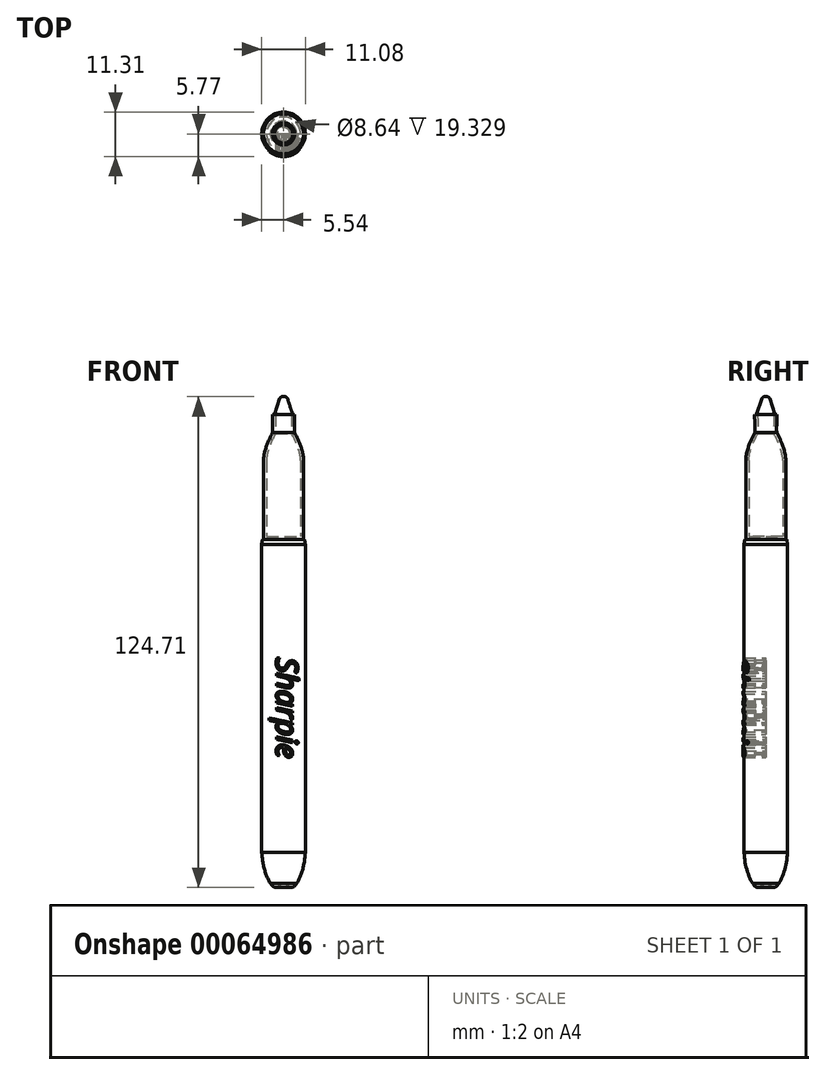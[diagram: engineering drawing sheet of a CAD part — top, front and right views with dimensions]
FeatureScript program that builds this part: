
annotation { "Feature Type Name" : "Feature", "Feature Type Description" : "" }
export const myFeature = defineFeature(function(context is Context, id is Id, definition is map)
    precondition{}
    {
        {
            var Q0;
            Q0=qCreatedBy(makeId("Right.planeOp"),FACE);
            var sketch = newSketch(context, id + "F0", { "sketchPlane" : qUnion([Q0])});
            skArc(sketch, "E0", {"start": v(1.65, 0) * mm, "mid": v(0.9, 0.63) * mm, "end": v(0, 1.02) * mm});
            skLineSegment(sketch, "E1", {"start": v(0, 0) * mm, "end": v(0, 15.3) * mm, "construction": true});
            skLineSegment(sketch, "E2", {"start": v(-4.14, 8.9) * mm, "end": v(12.15, 8.9) * mm, "construction": true});
            skLineSegment(sketch, "E3", {"start": v(5.54, -3.16) * mm, "end": v(5.54, 13.42) * mm, "construction": true});
            skLineSegment(sketch, "E4", {"start": v(3.31, 16.2) * mm, "end": v(3.31, -2.19) * mm, "construction": true});
            skFitSpline(sketch, "E5", {"points": [v(1.65, 0) * mm, v(3.31, 1.03) * mm], "startDerivative": vector(2.74, 0) * mm, "endDerivative": vector(1.4, 2.31) * mm});
            skFitSpline(sketch, "E6", {"points": [v(3.31, 1.03) * mm, v(5.54, 8.9) * mm], "startDerivative": vector(3.92, 5.98) * mm, "endDerivative": vector(0.67, 9.24) * mm});
            skLineSegment(sketch, "E7", {"start": v(-15.24, 87.12) * mm, "end": v(35.45, 87.12) * mm, "construction": true});
            skLineSegment(sketch, "E8", {"start": v(5.54, 8.9) * mm, "end": v(5.54, 87.12) * mm});
            skPoint(sketch, "E8.endSnap0", {"position": v(10.1, 87.12) * mm});
            skLineSegment(sketch, "E9", {"start": v(5.54, 87.12) * mm, "end": v(5.33, 88.38) * mm});
            skLineSegment(sketch, "E10", {"start": v(5.33, 88.38) * mm, "end": v(0, 88.38) * mm});
            skLineSegment(sketch, "E11", {"start": v(0, 88.38) * mm, "end": v(0, 1.02) * mm});
            skSolve(sketch);
        }
        {
            var Q0;
            Q0 = qSketchRegion(id + "F0", true);
            var Q1;
            Q1=sQuery(id+"F0.wireOp",EDGE,"E11");
            revolve(context, id + "F1", {"entities" : qUnion([Q0]), "axis" : qUnion([Q1]), "revolveType" : RevolveType.FULL});
        }
        {
            var Q0;
            Q0=qCreatedBy(makeId("Front.planeOp"),FACE);
            var sketch = newSketch(context, id + "F2", { "sketchPlane" : qUnion([Q0])});
            skLineSegment(sketch, "E12", {"start": v(0, 88.38) * mm, "end": v(0, 120.13) * mm});
            skLineSegment(sketch, "E13", {"start": v(0, 120.13) * mm, "end": v(2.8, 120.13) * mm});
            skLineSegment(sketch, "E14", {"start": v(-7.77, 108.47) * mm, "end": v(20.65, 108.47) * mm, "construction": true});
            skLineSegment(sketch, "E15", {"start": v(5.08, 128.73) * mm, "end": v(5.08, 79.74) * mm, "construction": true});
            skLineSegment(sketch, "E16", {"start": v(5.08, 79.74) * mm, "end": v(5.61, 79.74) * mm, "construction": true});
            skLineSegment(sketch, "E17", {"start": v(0, 88.38) * mm, "end": v(5.08, 88.38) * mm});
            skLineSegment(sketch, "E18", {"start": v(5.08, 88.38) * mm, "end": v(5.08, 108.47) * mm});
            skFitSpline(sketch, "E19", {"points": [v(2.8, 115.55) * mm, v(5.08, 108.47) * mm], "startDerivative": vector(4.16, -7.76) * mm, "endDerivative": vector(0, -5.98) * mm});
            skFitSpline(sketch, "E20", {"points": [v(2.8, 120.13) * mm, v(2.8, 115.55) * mm], "startDerivative": vector(0.35, -1.11) * mm, "endDerivative": vector(0.39, -3.2) * mm});
            skSolve(sketch);
        }
        {
            var Q0;
            Q0=makeQuery(id+"F2.imprint","IMPRINT",FACE,{"disambiguationData":[TD([[makeQuery(id+"F2.imprint","IMPRINT",EDGE,{"derivedFrom":sQuery(id+"F2.wireOp",EDGE,"E12")}),-1.0]])]});
            var Q1;
            Q1=sQuery(id+"F2.wireOp",EDGE,"E12");
            revolve(context, id + "F3", {"entities" : qUnion([Q0]), "axis" : qUnion([Q1]), "revolveType" : RevolveType.FULL});
        }
        {
            var Q0;
            Q0=makeQuery(id+"F3.opRevolve","SWEPT_FACE",FACE,{"disambiguationData":[OSD([sQuery(id+"F2.wireOp",EDGE,"E13")])]});
            shell(context, id + "F4", {"entities" : qUnion([Q0]), "thickness" : 0.76 * mm});
        }
        {
            var Q0;
            Q0=qCreatedBy(makeId("Front.planeOp"),FACE);
            var sketch = newSketch(context, id + "F5", { "sketchPlane" : qUnion([Q0])});
            skText(sketch, "E21", { "text": "Sharpie", "fontName": "OpenSans-Italic.ttf"});
            const initialGuessF5  = {"E21": [-0.00997, 0.02356, 1, 0, 0.00548]};
            skSetInitialGuess(sketch, initialGuessF5);
            skSolve(sketch);
        }
        {
            var Q0;
            Q0 = qSketchRegion(id + "F5", true);
            extrude(context, id + "F6", {"entities" : qUnion([Q0]), "depth" : 6.35 * mm});
        }
        {
            var Q0;
            Q0=qCreatedBy(makeId("Front.planeOp"),FACE);
            var sketch = newSketch(context, id + "F7", { "sketchPlane" : qUnion([Q0])});
            skLineSegment(sketch, "E22", {"start": v(0, 0) * mm, "end": v(0, 153.56) * mm, "construction": true});
            skLineSegment(sketch, "E23", {"start": v(0, 0) * mm, "end": v(-98.51, 0) * mm, "construction": true});
            skSolve(sketch);
        }
        {
            var Q0;
            Q0=qCreatedBy(makeId("Top.planeOp"),FACE);
            var sketch = newSketch(context, id + "F8", { "sketchPlane" : qUnion([Q0])});
            skLineSegment(sketch, "E24", {"start": v(0, 0) * mm, "end": v(0, 70.55) * mm, "construction": true});
            skSolve(sketch);
        }
        {
            var Q0;
            Q0=makeQuery(id+"F6.opExtrude","SWEPT_BODY",BODY,{"disambiguationData":[OSD([sQuery(id+"F5.wireOp",EDGE,"E21.sketch_text.stroke-126"),sQuery(id+"F5.wireOp",EDGE,"E21.sketch_text.stroke-127"),sQuery(id+"F5.wireOp",EDGE,"E21.sketch_text.stroke-128"),sQuery(id+"F5.wireOp",EDGE,"E21.sketch_text.stroke-129"),sQuery(id+"F5.wireOp",EDGE,"E21.sketch_text.stroke-130"),sQuery(id+"F5.wireOp",EDGE,"E21.sketch_text.stroke-131"),sQuery(id+"F5.wireOp",EDGE,"E21.sketch_text.stroke-132"),sQuery(id+"F5.wireOp",EDGE,"E21.sketch_text.stroke-133"),sQuery(id+"F5.wireOp",EDGE,"E21.sketch_text.stroke-134"),sQuery(id+"F5.wireOp",EDGE,"E21.sketch_text.stroke-135"),sQuery(id+"F5.wireOp",EDGE,"E21.sketch_text.stroke-136"),sQuery(id+"F5.wireOp",EDGE,"E21.sketch_text.stroke-137"),sQuery(id+"F5.wireOp",EDGE,"E21.sketch_text.stroke-138"),sQuery(id+"F5.wireOp",EDGE,"E21.sketch_text.stroke-139"),sQuery(id+"F5.wireOp",EDGE,"E21.sketch_text.stroke-140"),sQuery(id+"F5.wireOp",EDGE,"E21.sketch_text.stroke-141"),sQuery(id+"F5.wireOp",EDGE,"E21.sketch_text.stroke-142"),sQuery(id+"F5.wireOp",EDGE,"E21.sketch_text.stroke-143"),sQuery(id+"F5.wireOp",EDGE,"E21.sketch_text.stroke-144"),sQuery(id+"F5.wireOp",EDGE,"E21.sketch_text.stroke-145"),sQuery(id+"F5.wireOp",EDGE,"E21.sketch_text.stroke-146"),sQuery(id+"F5.wireOp",EDGE,"E21.sketch_text.stroke-147"),sQuery(id+"F5.wireOp",EDGE,"E21.sketch_text.stroke-148"),sQuery(id+"F5.wireOp",EDGE,"E21.sketch_text.stroke-149"),sQuery(id+"F5.wireOp",EDGE,"E21.sketch_text.stroke-150")])]});
            var Q1;
            Q1=makeQuery(id+"F6.opExtrude","SWEPT_BODY",BODY,{"disambiguationData":[OSD([sQuery(id+"F5.wireOp",EDGE,"E21.sketch_text.stroke-119"),sQuery(id+"F5.wireOp",EDGE,"E21.sketch_text.stroke-120"),sQuery(id+"F5.wireOp",EDGE,"E21.sketch_text.stroke-121"),sQuery(id+"F5.wireOp",EDGE,"E21.sketch_text.stroke-122"),sQuery(id+"F5.wireOp",EDGE,"E21.sketch_text.stroke-123"),sQuery(id+"F5.wireOp",EDGE,"E21.sketch_text.stroke-124"),sQuery(id+"F5.wireOp",EDGE,"E21.sketch_text.stroke-125")])]});
            var Q2;
            Q2=makeQuery(id+"F6.opExtrude","SWEPT_BODY",BODY,{"disambiguationData":[OSD([sQuery(id+"F5.wireOp",EDGE,"E21.sketch_text.stroke-115"),sQuery(id+"F5.wireOp",EDGE,"E21.sketch_text.stroke-116"),sQuery(id+"F5.wireOp",EDGE,"E21.sketch_text.stroke-117"),sQuery(id+"F5.wireOp",EDGE,"E21.sketch_text.stroke-118")])]});
            var Q3;
            Q3=makeQuery(id+"F6.opExtrude","SWEPT_BODY",BODY,{"disambiguationData":[OSD([sQuery(id+"F5.wireOp",EDGE,"E21.sketch_text.stroke-89"),sQuery(id+"F5.wireOp",EDGE,"E21.sketch_text.stroke-90"),sQuery(id+"F5.wireOp",EDGE,"E21.sketch_text.stroke-91"),sQuery(id+"F5.wireOp",EDGE,"E21.sketch_text.stroke-92"),sQuery(id+"F5.wireOp",EDGE,"E21.sketch_text.stroke-93"),sQuery(id+"F5.wireOp",EDGE,"E21.sketch_text.stroke-94"),sQuery(id+"F5.wireOp",EDGE,"E21.sketch_text.stroke-95"),sQuery(id+"F5.wireOp",EDGE,"E21.sketch_text.stroke-96"),sQuery(id+"F5.wireOp",EDGE,"E21.sketch_text.stroke-97"),sQuery(id+"F5.wireOp",EDGE,"E21.sketch_text.stroke-98"),sQuery(id+"F5.wireOp",EDGE,"E21.sketch_text.stroke-99"),sQuery(id+"F5.wireOp",EDGE,"E21.sketch_text.stroke-100"),sQuery(id+"F5.wireOp",EDGE,"E21.sketch_text.stroke-101"),sQuery(id+"F5.wireOp",EDGE,"E21.sketch_text.stroke-102"),sQuery(id+"F5.wireOp",EDGE,"E21.sketch_text.stroke-103"),sQuery(id+"F5.wireOp",EDGE,"E21.sketch_text.stroke-104"),sQuery(id+"F5.wireOp",EDGE,"E21.sketch_text.stroke-105"),sQuery(id+"F5.wireOp",EDGE,"E21.sketch_text.stroke-106"),sQuery(id+"F5.wireOp",EDGE,"E21.sketch_text.stroke-107"),sQuery(id+"F5.wireOp",EDGE,"E21.sketch_text.stroke-108"),sQuery(id+"F5.wireOp",EDGE,"E21.sketch_text.stroke-109"),sQuery(id+"F5.wireOp",EDGE,"E21.sketch_text.stroke-110"),sQuery(id+"F5.wireOp",EDGE,"E21.sketch_text.stroke-111"),sQuery(id+"F5.wireOp",EDGE,"E21.sketch_text.stroke-112"),sQuery(id+"F5.wireOp",EDGE,"E21.sketch_text.stroke-113"),sQuery(id+"F5.wireOp",EDGE,"E21.sketch_text.stroke-114")])]});
            var Q4;
            Q4=makeQuery(id+"F6.opExtrude","SWEPT_BODY",BODY,{"disambiguationData":[OSD([sQuery(id+"F5.wireOp",EDGE,"E21.sketch_text.stroke-74"),sQuery(id+"F5.wireOp",EDGE,"E21.sketch_text.stroke-75"),sQuery(id+"F5.wireOp",EDGE,"E21.sketch_text.stroke-76"),sQuery(id+"F5.wireOp",EDGE,"E21.sketch_text.stroke-77"),sQuery(id+"F5.wireOp",EDGE,"E21.sketch_text.stroke-78"),sQuery(id+"F5.wireOp",EDGE,"E21.sketch_text.stroke-79"),sQuery(id+"F5.wireOp",EDGE,"E21.sketch_text.stroke-80"),sQuery(id+"F5.wireOp",EDGE,"E21.sketch_text.stroke-81"),sQuery(id+"F5.wireOp",EDGE,"E21.sketch_text.stroke-82"),sQuery(id+"F5.wireOp",EDGE,"E21.sketch_text.stroke-83"),sQuery(id+"F5.wireOp",EDGE,"E21.sketch_text.stroke-84"),sQuery(id+"F5.wireOp",EDGE,"E21.sketch_text.stroke-85"),sQuery(id+"F5.wireOp",EDGE,"E21.sketch_text.stroke-86"),sQuery(id+"F5.wireOp",EDGE,"E21.sketch_text.stroke-87"),sQuery(id+"F5.wireOp",EDGE,"E21.sketch_text.stroke-88")])]});
            var Q5;
            Q5=makeQuery(id+"F6.opExtrude","SWEPT_BODY",BODY,{"disambiguationData":[OSD([sQuery(id+"F5.wireOp",EDGE,"E21.sketch_text.stroke-49"),sQuery(id+"F5.wireOp",EDGE,"E21.sketch_text.stroke-50"),sQuery(id+"F5.wireOp",EDGE,"E21.sketch_text.stroke-51"),sQuery(id+"F5.wireOp",EDGE,"E21.sketch_text.stroke-52"),sQuery(id+"F5.wireOp",EDGE,"E21.sketch_text.stroke-53"),sQuery(id+"F5.wireOp",EDGE,"E21.sketch_text.stroke-54"),sQuery(id+"F5.wireOp",EDGE,"E21.sketch_text.stroke-55"),sQuery(id+"F5.wireOp",EDGE,"E21.sketch_text.stroke-56"),sQuery(id+"F5.wireOp",EDGE,"E21.sketch_text.stroke-57"),sQuery(id+"F5.wireOp",EDGE,"E21.sketch_text.stroke-58"),sQuery(id+"F5.wireOp",EDGE,"E21.sketch_text.stroke-59"),sQuery(id+"F5.wireOp",EDGE,"E21.sketch_text.stroke-60"),sQuery(id+"F5.wireOp",EDGE,"E21.sketch_text.stroke-61"),sQuery(id+"F5.wireOp",EDGE,"E21.sketch_text.stroke-62"),sQuery(id+"F5.wireOp",EDGE,"E21.sketch_text.stroke-63"),sQuery(id+"F5.wireOp",EDGE,"E21.sketch_text.stroke-64"),sQuery(id+"F5.wireOp",EDGE,"E21.sketch_text.stroke-65"),sQuery(id+"F5.wireOp",EDGE,"E21.sketch_text.stroke-66"),sQuery(id+"F5.wireOp",EDGE,"E21.sketch_text.stroke-67"),sQuery(id+"F5.wireOp",EDGE,"E21.sketch_text.stroke-68"),sQuery(id+"F5.wireOp",EDGE,"E21.sketch_text.stroke-69"),sQuery(id+"F5.wireOp",EDGE,"E21.sketch_text.stroke-70"),sQuery(id+"F5.wireOp",EDGE,"E21.sketch_text.stroke-71"),sQuery(id+"F5.wireOp",EDGE,"E21.sketch_text.stroke-72"),sQuery(id+"F5.wireOp",EDGE,"E21.sketch_text.stroke-73")])]});
            var Q6;
            Q6=makeQuery(id+"F6.opExtrude","SWEPT_BODY",BODY,{"disambiguationData":[OSD([sQuery(id+"F5.wireOp",EDGE,"E21.sketch_text.stroke-27"),sQuery(id+"F5.wireOp",EDGE,"E21.sketch_text.stroke-28"),sQuery(id+"F5.wireOp",EDGE,"E21.sketch_text.stroke-29"),sQuery(id+"F5.wireOp",EDGE,"E21.sketch_text.stroke-30"),sQuery(id+"F5.wireOp",EDGE,"E21.sketch_text.stroke-31"),sQuery(id+"F5.wireOp",EDGE,"E21.sketch_text.stroke-32"),sQuery(id+"F5.wireOp",EDGE,"E21.sketch_text.stroke-33"),sQuery(id+"F5.wireOp",EDGE,"E21.sketch_text.stroke-34"),sQuery(id+"F5.wireOp",EDGE,"E21.sketch_text.stroke-35"),sQuery(id+"F5.wireOp",EDGE,"E21.sketch_text.stroke-36"),sQuery(id+"F5.wireOp",EDGE,"E21.sketch_text.stroke-37"),sQuery(id+"F5.wireOp",EDGE,"E21.sketch_text.stroke-38"),sQuery(id+"F5.wireOp",EDGE,"E21.sketch_text.stroke-39"),sQuery(id+"F5.wireOp",EDGE,"E21.sketch_text.stroke-40"),sQuery(id+"F5.wireOp",EDGE,"E21.sketch_text.stroke-41"),sQuery(id+"F5.wireOp",EDGE,"E21.sketch_text.stroke-42"),sQuery(id+"F5.wireOp",EDGE,"E21.sketch_text.stroke-43"),sQuery(id+"F5.wireOp",EDGE,"E21.sketch_text.stroke-44"),sQuery(id+"F5.wireOp",EDGE,"E21.sketch_text.stroke-45"),sQuery(id+"F5.wireOp",EDGE,"E21.sketch_text.stroke-46"),sQuery(id+"F5.wireOp",EDGE,"E21.sketch_text.stroke-47"),sQuery(id+"F5.wireOp",EDGE,"E21.sketch_text.stroke-48")])]});
            var Q7;
            Q7=makeQuery(id+"F6.opExtrude","SWEPT_BODY",BODY,{"disambiguationData":[OSD([sQuery(id+"F5.wireOp",EDGE,"E21.sketch_text.stroke-0"),sQuery(id+"F5.wireOp",EDGE,"E21.sketch_text.stroke-1"),sQuery(id+"F5.wireOp",EDGE,"E21.sketch_text.stroke-2"),sQuery(id+"F5.wireOp",EDGE,"E21.sketch_text.stroke-3"),sQuery(id+"F5.wireOp",EDGE,"E21.sketch_text.stroke-4"),sQuery(id+"F5.wireOp",EDGE,"E21.sketch_text.stroke-5"),sQuery(id+"F5.wireOp",EDGE,"E21.sketch_text.stroke-6"),sQuery(id+"F5.wireOp",EDGE,"E21.sketch_text.stroke-7"),sQuery(id+"F5.wireOp",EDGE,"E21.sketch_text.stroke-8"),sQuery(id+"F5.wireOp",EDGE,"E21.sketch_text.stroke-9"),sQuery(id+"F5.wireOp",EDGE,"E21.sketch_text.stroke-10"),sQuery(id+"F5.wireOp",EDGE,"E21.sketch_text.stroke-11"),sQuery(id+"F5.wireOp",EDGE,"E21.sketch_text.stroke-12"),sQuery(id+"F5.wireOp",EDGE,"E21.sketch_text.stroke-13"),sQuery(id+"F5.wireOp",EDGE,"E21.sketch_text.stroke-14"),sQuery(id+"F5.wireOp",EDGE,"E21.sketch_text.stroke-15"),sQuery(id+"F5.wireOp",EDGE,"E21.sketch_text.stroke-16"),sQuery(id+"F5.wireOp",EDGE,"E21.sketch_text.stroke-17"),sQuery(id+"F5.wireOp",EDGE,"E21.sketch_text.stroke-18"),sQuery(id+"F5.wireOp",EDGE,"E21.sketch_text.stroke-19"),sQuery(id+"F5.wireOp",EDGE,"E21.sketch_text.stroke-20"),sQuery(id+"F5.wireOp",EDGE,"E21.sketch_text.stroke-21"),sQuery(id+"F5.wireOp",EDGE,"E21.sketch_text.stroke-22"),sQuery(id+"F5.wireOp",EDGE,"E21.sketch_text.stroke-23"),sQuery(id+"F5.wireOp",EDGE,"E21.sketch_text.stroke-24"),sQuery(id+"F5.wireOp",EDGE,"E21.sketch_text.stroke-25"),sQuery(id+"F5.wireOp",EDGE,"E21.sketch_text.stroke-26")])]});
            var Q8;
            Q8=sQuery(id+"F8.wireOp",EDGE,"E24");
            transform(context, id + "F9", {"entities" : qUnion([Q0, Q1, Q2, Q3, Q4, Q5, Q6, Q7]), "transformType" : TransformType.ROTATION, "transformAxis" : qUnion([Q8]), "angle" : 90 * degree, "makeCopy" : false});
        }
        {
            var Q0;
            Q0=makeQuery(id+"F6.opExtrude","SWEPT_BODY",BODY,{"disambiguationData":[OSD([sQuery(id+"F5.wireOp",EDGE,"E21.sketch_text.stroke-0"),sQuery(id+"F5.wireOp",EDGE,"E21.sketch_text.stroke-1"),sQuery(id+"F5.wireOp",EDGE,"E21.sketch_text.stroke-2"),sQuery(id+"F5.wireOp",EDGE,"E21.sketch_text.stroke-3"),sQuery(id+"F5.wireOp",EDGE,"E21.sketch_text.stroke-4"),sQuery(id+"F5.wireOp",EDGE,"E21.sketch_text.stroke-5"),sQuery(id+"F5.wireOp",EDGE,"E21.sketch_text.stroke-6"),sQuery(id+"F5.wireOp",EDGE,"E21.sketch_text.stroke-7"),sQuery(id+"F5.wireOp",EDGE,"E21.sketch_text.stroke-8"),sQuery(id+"F5.wireOp",EDGE,"E21.sketch_text.stroke-9"),sQuery(id+"F5.wireOp",EDGE,"E21.sketch_text.stroke-10"),sQuery(id+"F5.wireOp",EDGE,"E21.sketch_text.stroke-11"),sQuery(id+"F5.wireOp",EDGE,"E21.sketch_text.stroke-12"),sQuery(id+"F5.wireOp",EDGE,"E21.sketch_text.stroke-13"),sQuery(id+"F5.wireOp",EDGE,"E21.sketch_text.stroke-14"),sQuery(id+"F5.wireOp",EDGE,"E21.sketch_text.stroke-15"),sQuery(id+"F5.wireOp",EDGE,"E21.sketch_text.stroke-16"),sQuery(id+"F5.wireOp",EDGE,"E21.sketch_text.stroke-17"),sQuery(id+"F5.wireOp",EDGE,"E21.sketch_text.stroke-18"),sQuery(id+"F5.wireOp",EDGE,"E21.sketch_text.stroke-19"),sQuery(id+"F5.wireOp",EDGE,"E21.sketch_text.stroke-20"),sQuery(id+"F5.wireOp",EDGE,"E21.sketch_text.stroke-21"),sQuery(id+"F5.wireOp",EDGE,"E21.sketch_text.stroke-22"),sQuery(id+"F5.wireOp",EDGE,"E21.sketch_text.stroke-23"),sQuery(id+"F5.wireOp",EDGE,"E21.sketch_text.stroke-24"),sQuery(id+"F5.wireOp",EDGE,"E21.sketch_text.stroke-25"),sQuery(id+"F5.wireOp",EDGE,"E21.sketch_text.stroke-26")])]});
            var Q1;
            Q1=makeQuery(id+"F6.opExtrude","SWEPT_BODY",BODY,{"disambiguationData":[OSD([sQuery(id+"F5.wireOp",EDGE,"E21.sketch_text.stroke-27"),sQuery(id+"F5.wireOp",EDGE,"E21.sketch_text.stroke-28"),sQuery(id+"F5.wireOp",EDGE,"E21.sketch_text.stroke-29"),sQuery(id+"F5.wireOp",EDGE,"E21.sketch_text.stroke-30"),sQuery(id+"F5.wireOp",EDGE,"E21.sketch_text.stroke-31"),sQuery(id+"F5.wireOp",EDGE,"E21.sketch_text.stroke-32"),sQuery(id+"F5.wireOp",EDGE,"E21.sketch_text.stroke-33"),sQuery(id+"F5.wireOp",EDGE,"E21.sketch_text.stroke-34"),sQuery(id+"F5.wireOp",EDGE,"E21.sketch_text.stroke-35"),sQuery(id+"F5.wireOp",EDGE,"E21.sketch_text.stroke-36"),sQuery(id+"F5.wireOp",EDGE,"E21.sketch_text.stroke-37"),sQuery(id+"F5.wireOp",EDGE,"E21.sketch_text.stroke-38"),sQuery(id+"F5.wireOp",EDGE,"E21.sketch_text.stroke-39"),sQuery(id+"F5.wireOp",EDGE,"E21.sketch_text.stroke-40"),sQuery(id+"F5.wireOp",EDGE,"E21.sketch_text.stroke-41"),sQuery(id+"F5.wireOp",EDGE,"E21.sketch_text.stroke-42"),sQuery(id+"F5.wireOp",EDGE,"E21.sketch_text.stroke-43"),sQuery(id+"F5.wireOp",EDGE,"E21.sketch_text.stroke-44"),sQuery(id+"F5.wireOp",EDGE,"E21.sketch_text.stroke-45"),sQuery(id+"F5.wireOp",EDGE,"E21.sketch_text.stroke-46"),sQuery(id+"F5.wireOp",EDGE,"E21.sketch_text.stroke-47"),sQuery(id+"F5.wireOp",EDGE,"E21.sketch_text.stroke-48")])]});
            var Q2;
            Q2=makeQuery(id+"F6.opExtrude","SWEPT_BODY",BODY,{"disambiguationData":[OSD([sQuery(id+"F5.wireOp",EDGE,"E21.sketch_text.stroke-49"),sQuery(id+"F5.wireOp",EDGE,"E21.sketch_text.stroke-50"),sQuery(id+"F5.wireOp",EDGE,"E21.sketch_text.stroke-51"),sQuery(id+"F5.wireOp",EDGE,"E21.sketch_text.stroke-52"),sQuery(id+"F5.wireOp",EDGE,"E21.sketch_text.stroke-53"),sQuery(id+"F5.wireOp",EDGE,"E21.sketch_text.stroke-54"),sQuery(id+"F5.wireOp",EDGE,"E21.sketch_text.stroke-55"),sQuery(id+"F5.wireOp",EDGE,"E21.sketch_text.stroke-56"),sQuery(id+"F5.wireOp",EDGE,"E21.sketch_text.stroke-57"),sQuery(id+"F5.wireOp",EDGE,"E21.sketch_text.stroke-58"),sQuery(id+"F5.wireOp",EDGE,"E21.sketch_text.stroke-59"),sQuery(id+"F5.wireOp",EDGE,"E21.sketch_text.stroke-60"),sQuery(id+"F5.wireOp",EDGE,"E21.sketch_text.stroke-61"),sQuery(id+"F5.wireOp",EDGE,"E21.sketch_text.stroke-62"),sQuery(id+"F5.wireOp",EDGE,"E21.sketch_text.stroke-63"),sQuery(id+"F5.wireOp",EDGE,"E21.sketch_text.stroke-64"),sQuery(id+"F5.wireOp",EDGE,"E21.sketch_text.stroke-65"),sQuery(id+"F5.wireOp",EDGE,"E21.sketch_text.stroke-66"),sQuery(id+"F5.wireOp",EDGE,"E21.sketch_text.stroke-67"),sQuery(id+"F5.wireOp",EDGE,"E21.sketch_text.stroke-68"),sQuery(id+"F5.wireOp",EDGE,"E21.sketch_text.stroke-69"),sQuery(id+"F5.wireOp",EDGE,"E21.sketch_text.stroke-70"),sQuery(id+"F5.wireOp",EDGE,"E21.sketch_text.stroke-71"),sQuery(id+"F5.wireOp",EDGE,"E21.sketch_text.stroke-72"),sQuery(id+"F5.wireOp",EDGE,"E21.sketch_text.stroke-73")])]});
            var Q3;
            Q3=makeQuery(id+"F6.opExtrude","SWEPT_BODY",BODY,{"disambiguationData":[OSD([sQuery(id+"F5.wireOp",EDGE,"E21.sketch_text.stroke-74"),sQuery(id+"F5.wireOp",EDGE,"E21.sketch_text.stroke-75"),sQuery(id+"F5.wireOp",EDGE,"E21.sketch_text.stroke-76"),sQuery(id+"F5.wireOp",EDGE,"E21.sketch_text.stroke-77"),sQuery(id+"F5.wireOp",EDGE,"E21.sketch_text.stroke-78"),sQuery(id+"F5.wireOp",EDGE,"E21.sketch_text.stroke-79"),sQuery(id+"F5.wireOp",EDGE,"E21.sketch_text.stroke-80"),sQuery(id+"F5.wireOp",EDGE,"E21.sketch_text.stroke-81"),sQuery(id+"F5.wireOp",EDGE,"E21.sketch_text.stroke-82"),sQuery(id+"F5.wireOp",EDGE,"E21.sketch_text.stroke-83"),sQuery(id+"F5.wireOp",EDGE,"E21.sketch_text.stroke-84"),sQuery(id+"F5.wireOp",EDGE,"E21.sketch_text.stroke-85"),sQuery(id+"F5.wireOp",EDGE,"E21.sketch_text.stroke-86"),sQuery(id+"F5.wireOp",EDGE,"E21.sketch_text.stroke-87"),sQuery(id+"F5.wireOp",EDGE,"E21.sketch_text.stroke-88")])]});
            var Q4;
            Q4=makeQuery(id+"F6.opExtrude","SWEPT_BODY",BODY,{"disambiguationData":[OSD([sQuery(id+"F5.wireOp",EDGE,"E21.sketch_text.stroke-89"),sQuery(id+"F5.wireOp",EDGE,"E21.sketch_text.stroke-90"),sQuery(id+"F5.wireOp",EDGE,"E21.sketch_text.stroke-91"),sQuery(id+"F5.wireOp",EDGE,"E21.sketch_text.stroke-92"),sQuery(id+"F5.wireOp",EDGE,"E21.sketch_text.stroke-93"),sQuery(id+"F5.wireOp",EDGE,"E21.sketch_text.stroke-94"),sQuery(id+"F5.wireOp",EDGE,"E21.sketch_text.stroke-95"),sQuery(id+"F5.wireOp",EDGE,"E21.sketch_text.stroke-96"),sQuery(id+"F5.wireOp",EDGE,"E21.sketch_text.stroke-97"),sQuery(id+"F5.wireOp",EDGE,"E21.sketch_text.stroke-98"),sQuery(id+"F5.wireOp",EDGE,"E21.sketch_text.stroke-99"),sQuery(id+"F5.wireOp",EDGE,"E21.sketch_text.stroke-100"),sQuery(id+"F5.wireOp",EDGE,"E21.sketch_text.stroke-101"),sQuery(id+"F5.wireOp",EDGE,"E21.sketch_text.stroke-102"),sQuery(id+"F5.wireOp",EDGE,"E21.sketch_text.stroke-103"),sQuery(id+"F5.wireOp",EDGE,"E21.sketch_text.stroke-104"),sQuery(id+"F5.wireOp",EDGE,"E21.sketch_text.stroke-105"),sQuery(id+"F5.wireOp",EDGE,"E21.sketch_text.stroke-106"),sQuery(id+"F5.wireOp",EDGE,"E21.sketch_text.stroke-107"),sQuery(id+"F5.wireOp",EDGE,"E21.sketch_text.stroke-108"),sQuery(id+"F5.wireOp",EDGE,"E21.sketch_text.stroke-109"),sQuery(id+"F5.wireOp",EDGE,"E21.sketch_text.stroke-110"),sQuery(id+"F5.wireOp",EDGE,"E21.sketch_text.stroke-111"),sQuery(id+"F5.wireOp",EDGE,"E21.sketch_text.stroke-112"),sQuery(id+"F5.wireOp",EDGE,"E21.sketch_text.stroke-113"),sQuery(id+"F5.wireOp",EDGE,"E21.sketch_text.stroke-114")])]});
            var Q5;
            Q5=makeQuery(id+"F6.opExtrude","SWEPT_BODY",BODY,{"disambiguationData":[OSD([sQuery(id+"F5.wireOp",EDGE,"E21.sketch_text.stroke-115"),sQuery(id+"F5.wireOp",EDGE,"E21.sketch_text.stroke-116"),sQuery(id+"F5.wireOp",EDGE,"E21.sketch_text.stroke-117"),sQuery(id+"F5.wireOp",EDGE,"E21.sketch_text.stroke-118")])]});
            var Q6;
            Q6=makeQuery(id+"F6.opExtrude","SWEPT_BODY",BODY,{"disambiguationData":[OSD([sQuery(id+"F5.wireOp",EDGE,"E21.sketch_text.stroke-119"),sQuery(id+"F5.wireOp",EDGE,"E21.sketch_text.stroke-120"),sQuery(id+"F5.wireOp",EDGE,"E21.sketch_text.stroke-121"),sQuery(id+"F5.wireOp",EDGE,"E21.sketch_text.stroke-122"),sQuery(id+"F5.wireOp",EDGE,"E21.sketch_text.stroke-123"),sQuery(id+"F5.wireOp",EDGE,"E21.sketch_text.stroke-124"),sQuery(id+"F5.wireOp",EDGE,"E21.sketch_text.stroke-125")])]});
            var Q7;
            Q7=makeQuery(id+"F6.opExtrude","SWEPT_BODY",BODY,{"disambiguationData":[OSD([sQuery(id+"F5.wireOp",EDGE,"E21.sketch_text.stroke-126"),sQuery(id+"F5.wireOp",EDGE,"E21.sketch_text.stroke-127"),sQuery(id+"F5.wireOp",EDGE,"E21.sketch_text.stroke-128"),sQuery(id+"F5.wireOp",EDGE,"E21.sketch_text.stroke-129"),sQuery(id+"F5.wireOp",EDGE,"E21.sketch_text.stroke-130"),sQuery(id+"F5.wireOp",EDGE,"E21.sketch_text.stroke-131"),sQuery(id+"F5.wireOp",EDGE,"E21.sketch_text.stroke-132"),sQuery(id+"F5.wireOp",EDGE,"E21.sketch_text.stroke-133"),sQuery(id+"F5.wireOp",EDGE,"E21.sketch_text.stroke-134"),sQuery(id+"F5.wireOp",EDGE,"E21.sketch_text.stroke-135"),sQuery(id+"F5.wireOp",EDGE,"E21.sketch_text.stroke-136"),sQuery(id+"F5.wireOp",EDGE,"E21.sketch_text.stroke-137"),sQuery(id+"F5.wireOp",EDGE,"E21.sketch_text.stroke-138"),sQuery(id+"F5.wireOp",EDGE,"E21.sketch_text.stroke-139"),sQuery(id+"F5.wireOp",EDGE,"E21.sketch_text.stroke-140"),sQuery(id+"F5.wireOp",EDGE,"E21.sketch_text.stroke-141"),sQuery(id+"F5.wireOp",EDGE,"E21.sketch_text.stroke-142"),sQuery(id+"F5.wireOp",EDGE,"E21.sketch_text.stroke-143"),sQuery(id+"F5.wireOp",EDGE,"E21.sketch_text.stroke-144"),sQuery(id+"F5.wireOp",EDGE,"E21.sketch_text.stroke-145"),sQuery(id+"F5.wireOp",EDGE,"E21.sketch_text.stroke-146"),sQuery(id+"F5.wireOp",EDGE,"E21.sketch_text.stroke-147"),sQuery(id+"F5.wireOp",EDGE,"E21.sketch_text.stroke-148"),sQuery(id+"F5.wireOp",EDGE,"E21.sketch_text.stroke-149"),sQuery(id+"F5.wireOp",EDGE,"E21.sketch_text.stroke-150")])]});
            var Q8;
            Q8=sQuery(id+"F7.wireOp",EDGE,"E22");
            transform(context, id + "F10", {"entities" : qUnion([Q0, Q1, Q2, Q3, Q4, Q5, Q6, Q7]), "transformType" : TransformType.TRANSLATION_DISTANCE, "transformDirection" : qUnion([Q8]), "distance" : 48.47 * mm, "makeCopy" : false});
        }
        {
            var Q0;
            Q0=makeQuery(id+"F6.opExtrude","SWEPT_BODY",BODY,{"disambiguationData":[OSD([sQuery(id+"F5.wireOp",EDGE,"E21.sketch_text.stroke-126"),sQuery(id+"F5.wireOp",EDGE,"E21.sketch_text.stroke-127"),sQuery(id+"F5.wireOp",EDGE,"E21.sketch_text.stroke-128"),sQuery(id+"F5.wireOp",EDGE,"E21.sketch_text.stroke-129"),sQuery(id+"F5.wireOp",EDGE,"E21.sketch_text.stroke-130"),sQuery(id+"F5.wireOp",EDGE,"E21.sketch_text.stroke-131"),sQuery(id+"F5.wireOp",EDGE,"E21.sketch_text.stroke-132"),sQuery(id+"F5.wireOp",EDGE,"E21.sketch_text.stroke-133"),sQuery(id+"F5.wireOp",EDGE,"E21.sketch_text.stroke-134"),sQuery(id+"F5.wireOp",EDGE,"E21.sketch_text.stroke-135"),sQuery(id+"F5.wireOp",EDGE,"E21.sketch_text.stroke-136"),sQuery(id+"F5.wireOp",EDGE,"E21.sketch_text.stroke-137"),sQuery(id+"F5.wireOp",EDGE,"E21.sketch_text.stroke-138"),sQuery(id+"F5.wireOp",EDGE,"E21.sketch_text.stroke-139"),sQuery(id+"F5.wireOp",EDGE,"E21.sketch_text.stroke-140"),sQuery(id+"F5.wireOp",EDGE,"E21.sketch_text.stroke-141"),sQuery(id+"F5.wireOp",EDGE,"E21.sketch_text.stroke-142"),sQuery(id+"F5.wireOp",EDGE,"E21.sketch_text.stroke-143"),sQuery(id+"F5.wireOp",EDGE,"E21.sketch_text.stroke-144"),sQuery(id+"F5.wireOp",EDGE,"E21.sketch_text.stroke-145"),sQuery(id+"F5.wireOp",EDGE,"E21.sketch_text.stroke-146"),sQuery(id+"F5.wireOp",EDGE,"E21.sketch_text.stroke-147"),sQuery(id+"F5.wireOp",EDGE,"E21.sketch_text.stroke-148"),sQuery(id+"F5.wireOp",EDGE,"E21.sketch_text.stroke-149"),sQuery(id+"F5.wireOp",EDGE,"E21.sketch_text.stroke-150")])]});
            var Q1;
            Q1=makeQuery(id+"F6.opExtrude","SWEPT_BODY",BODY,{"disambiguationData":[OSD([sQuery(id+"F5.wireOp",EDGE,"E21.sketch_text.stroke-119"),sQuery(id+"F5.wireOp",EDGE,"E21.sketch_text.stroke-120"),sQuery(id+"F5.wireOp",EDGE,"E21.sketch_text.stroke-121"),sQuery(id+"F5.wireOp",EDGE,"E21.sketch_text.stroke-122"),sQuery(id+"F5.wireOp",EDGE,"E21.sketch_text.stroke-123"),sQuery(id+"F5.wireOp",EDGE,"E21.sketch_text.stroke-124"),sQuery(id+"F5.wireOp",EDGE,"E21.sketch_text.stroke-125")])]});
            var Q2;
            Q2=makeQuery(id+"F6.opExtrude","SWEPT_BODY",BODY,{"disambiguationData":[OSD([sQuery(id+"F5.wireOp",EDGE,"E21.sketch_text.stroke-115"),sQuery(id+"F5.wireOp",EDGE,"E21.sketch_text.stroke-116"),sQuery(id+"F5.wireOp",EDGE,"E21.sketch_text.stroke-117"),sQuery(id+"F5.wireOp",EDGE,"E21.sketch_text.stroke-118")])]});
            var Q3;
            Q3=makeQuery(id+"F6.opExtrude","SWEPT_BODY",BODY,{"disambiguationData":[OSD([sQuery(id+"F5.wireOp",EDGE,"E21.sketch_text.stroke-89"),sQuery(id+"F5.wireOp",EDGE,"E21.sketch_text.stroke-90"),sQuery(id+"F5.wireOp",EDGE,"E21.sketch_text.stroke-91"),sQuery(id+"F5.wireOp",EDGE,"E21.sketch_text.stroke-92"),sQuery(id+"F5.wireOp",EDGE,"E21.sketch_text.stroke-93"),sQuery(id+"F5.wireOp",EDGE,"E21.sketch_text.stroke-94"),sQuery(id+"F5.wireOp",EDGE,"E21.sketch_text.stroke-95"),sQuery(id+"F5.wireOp",EDGE,"E21.sketch_text.stroke-96"),sQuery(id+"F5.wireOp",EDGE,"E21.sketch_text.stroke-97"),sQuery(id+"F5.wireOp",EDGE,"E21.sketch_text.stroke-98"),sQuery(id+"F5.wireOp",EDGE,"E21.sketch_text.stroke-99"),sQuery(id+"F5.wireOp",EDGE,"E21.sketch_text.stroke-100"),sQuery(id+"F5.wireOp",EDGE,"E21.sketch_text.stroke-101"),sQuery(id+"F5.wireOp",EDGE,"E21.sketch_text.stroke-102"),sQuery(id+"F5.wireOp",EDGE,"E21.sketch_text.stroke-103"),sQuery(id+"F5.wireOp",EDGE,"E21.sketch_text.stroke-104"),sQuery(id+"F5.wireOp",EDGE,"E21.sketch_text.stroke-105"),sQuery(id+"F5.wireOp",EDGE,"E21.sketch_text.stroke-106"),sQuery(id+"F5.wireOp",EDGE,"E21.sketch_text.stroke-107"),sQuery(id+"F5.wireOp",EDGE,"E21.sketch_text.stroke-108"),sQuery(id+"F5.wireOp",EDGE,"E21.sketch_text.stroke-109"),sQuery(id+"F5.wireOp",EDGE,"E21.sketch_text.stroke-110"),sQuery(id+"F5.wireOp",EDGE,"E21.sketch_text.stroke-111"),sQuery(id+"F5.wireOp",EDGE,"E21.sketch_text.stroke-112"),sQuery(id+"F5.wireOp",EDGE,"E21.sketch_text.stroke-113"),sQuery(id+"F5.wireOp",EDGE,"E21.sketch_text.stroke-114")])]});
            var Q4;
            Q4=makeQuery(id+"F6.opExtrude","SWEPT_BODY",BODY,{"disambiguationData":[OSD([sQuery(id+"F5.wireOp",EDGE,"E21.sketch_text.stroke-74"),sQuery(id+"F5.wireOp",EDGE,"E21.sketch_text.stroke-75"),sQuery(id+"F5.wireOp",EDGE,"E21.sketch_text.stroke-76"),sQuery(id+"F5.wireOp",EDGE,"E21.sketch_text.stroke-77"),sQuery(id+"F5.wireOp",EDGE,"E21.sketch_text.stroke-78"),sQuery(id+"F5.wireOp",EDGE,"E21.sketch_text.stroke-79"),sQuery(id+"F5.wireOp",EDGE,"E21.sketch_text.stroke-80"),sQuery(id+"F5.wireOp",EDGE,"E21.sketch_text.stroke-81"),sQuery(id+"F5.wireOp",EDGE,"E21.sketch_text.stroke-82"),sQuery(id+"F5.wireOp",EDGE,"E21.sketch_text.stroke-83"),sQuery(id+"F5.wireOp",EDGE,"E21.sketch_text.stroke-84"),sQuery(id+"F5.wireOp",EDGE,"E21.sketch_text.stroke-85"),sQuery(id+"F5.wireOp",EDGE,"E21.sketch_text.stroke-86"),sQuery(id+"F5.wireOp",EDGE,"E21.sketch_text.stroke-87"),sQuery(id+"F5.wireOp",EDGE,"E21.sketch_text.stroke-88")])]});
            var Q5;
            Q5=makeQuery(id+"F6.opExtrude","SWEPT_BODY",BODY,{"disambiguationData":[OSD([sQuery(id+"F5.wireOp",EDGE,"E21.sketch_text.stroke-49"),sQuery(id+"F5.wireOp",EDGE,"E21.sketch_text.stroke-50"),sQuery(id+"F5.wireOp",EDGE,"E21.sketch_text.stroke-51"),sQuery(id+"F5.wireOp",EDGE,"E21.sketch_text.stroke-52"),sQuery(id+"F5.wireOp",EDGE,"E21.sketch_text.stroke-53"),sQuery(id+"F5.wireOp",EDGE,"E21.sketch_text.stroke-54"),sQuery(id+"F5.wireOp",EDGE,"E21.sketch_text.stroke-55"),sQuery(id+"F5.wireOp",EDGE,"E21.sketch_text.stroke-56"),sQuery(id+"F5.wireOp",EDGE,"E21.sketch_text.stroke-57"),sQuery(id+"F5.wireOp",EDGE,"E21.sketch_text.stroke-58"),sQuery(id+"F5.wireOp",EDGE,"E21.sketch_text.stroke-59"),sQuery(id+"F5.wireOp",EDGE,"E21.sketch_text.stroke-60"),sQuery(id+"F5.wireOp",EDGE,"E21.sketch_text.stroke-61"),sQuery(id+"F5.wireOp",EDGE,"E21.sketch_text.stroke-62"),sQuery(id+"F5.wireOp",EDGE,"E21.sketch_text.stroke-63"),sQuery(id+"F5.wireOp",EDGE,"E21.sketch_text.stroke-64"),sQuery(id+"F5.wireOp",EDGE,"E21.sketch_text.stroke-65"),sQuery(id+"F5.wireOp",EDGE,"E21.sketch_text.stroke-66"),sQuery(id+"F5.wireOp",EDGE,"E21.sketch_text.stroke-67"),sQuery(id+"F5.wireOp",EDGE,"E21.sketch_text.stroke-68"),sQuery(id+"F5.wireOp",EDGE,"E21.sketch_text.stroke-69"),sQuery(id+"F5.wireOp",EDGE,"E21.sketch_text.stroke-70"),sQuery(id+"F5.wireOp",EDGE,"E21.sketch_text.stroke-71"),sQuery(id+"F5.wireOp",EDGE,"E21.sketch_text.stroke-72"),sQuery(id+"F5.wireOp",EDGE,"E21.sketch_text.stroke-73")])]});
            var Q6;
            Q6=makeQuery(id+"F6.opExtrude","SWEPT_BODY",BODY,{"disambiguationData":[OSD([sQuery(id+"F5.wireOp",EDGE,"E21.sketch_text.stroke-27"),sQuery(id+"F5.wireOp",EDGE,"E21.sketch_text.stroke-28"),sQuery(id+"F5.wireOp",EDGE,"E21.sketch_text.stroke-29"),sQuery(id+"F5.wireOp",EDGE,"E21.sketch_text.stroke-30"),sQuery(id+"F5.wireOp",EDGE,"E21.sketch_text.stroke-31"),sQuery(id+"F5.wireOp",EDGE,"E21.sketch_text.stroke-32"),sQuery(id+"F5.wireOp",EDGE,"E21.sketch_text.stroke-33"),sQuery(id+"F5.wireOp",EDGE,"E21.sketch_text.stroke-34"),sQuery(id+"F5.wireOp",EDGE,"E21.sketch_text.stroke-35"),sQuery(id+"F5.wireOp",EDGE,"E21.sketch_text.stroke-36"),sQuery(id+"F5.wireOp",EDGE,"E21.sketch_text.stroke-37"),sQuery(id+"F5.wireOp",EDGE,"E21.sketch_text.stroke-38"),sQuery(id+"F5.wireOp",EDGE,"E21.sketch_text.stroke-39"),sQuery(id+"F5.wireOp",EDGE,"E21.sketch_text.stroke-40"),sQuery(id+"F5.wireOp",EDGE,"E21.sketch_text.stroke-41"),sQuery(id+"F5.wireOp",EDGE,"E21.sketch_text.stroke-42"),sQuery(id+"F5.wireOp",EDGE,"E21.sketch_text.stroke-43"),sQuery(id+"F5.wireOp",EDGE,"E21.sketch_text.stroke-44"),sQuery(id+"F5.wireOp",EDGE,"E21.sketch_text.stroke-45"),sQuery(id+"F5.wireOp",EDGE,"E21.sketch_text.stroke-46"),sQuery(id+"F5.wireOp",EDGE,"E21.sketch_text.stroke-47"),sQuery(id+"F5.wireOp",EDGE,"E21.sketch_text.stroke-48")])]});
            var Q7;
            Q7=makeQuery(id+"F6.opExtrude","SWEPT_BODY",BODY,{"disambiguationData":[OSD([sQuery(id+"F5.wireOp",EDGE,"E21.sketch_text.stroke-0"),sQuery(id+"F5.wireOp",EDGE,"E21.sketch_text.stroke-1"),sQuery(id+"F5.wireOp",EDGE,"E21.sketch_text.stroke-2"),sQuery(id+"F5.wireOp",EDGE,"E21.sketch_text.stroke-3"),sQuery(id+"F5.wireOp",EDGE,"E21.sketch_text.stroke-4"),sQuery(id+"F5.wireOp",EDGE,"E21.sketch_text.stroke-5"),sQuery(id+"F5.wireOp",EDGE,"E21.sketch_text.stroke-6"),sQuery(id+"F5.wireOp",EDGE,"E21.sketch_text.stroke-7"),sQuery(id+"F5.wireOp",EDGE,"E21.sketch_text.stroke-8"),sQuery(id+"F5.wireOp",EDGE,"E21.sketch_text.stroke-9"),sQuery(id+"F5.wireOp",EDGE,"E21.sketch_text.stroke-10"),sQuery(id+"F5.wireOp",EDGE,"E21.sketch_text.stroke-11"),sQuery(id+"F5.wireOp",EDGE,"E21.sketch_text.stroke-12"),sQuery(id+"F5.wireOp",EDGE,"E21.sketch_text.stroke-13"),sQuery(id+"F5.wireOp",EDGE,"E21.sketch_text.stroke-14"),sQuery(id+"F5.wireOp",EDGE,"E21.sketch_text.stroke-15"),sQuery(id+"F5.wireOp",EDGE,"E21.sketch_text.stroke-16"),sQuery(id+"F5.wireOp",EDGE,"E21.sketch_text.stroke-17"),sQuery(id+"F5.wireOp",EDGE,"E21.sketch_text.stroke-18"),sQuery(id+"F5.wireOp",EDGE,"E21.sketch_text.stroke-19"),sQuery(id+"F5.wireOp",EDGE,"E21.sketch_text.stroke-20"),sQuery(id+"F5.wireOp",EDGE,"E21.sketch_text.stroke-21"),sQuery(id+"F5.wireOp",EDGE,"E21.sketch_text.stroke-22"),sQuery(id+"F5.wireOp",EDGE,"E21.sketch_text.stroke-23"),sQuery(id+"F5.wireOp",EDGE,"E21.sketch_text.stroke-24"),sQuery(id+"F5.wireOp",EDGE,"E21.sketch_text.stroke-25"),sQuery(id+"F5.wireOp",EDGE,"E21.sketch_text.stroke-26")])]});
            var Q8;
            Q8=sQuery(id+"F7.wireOp",EDGE,"E23");
            transform(context, id + "F11", {"entities" : qUnion([Q0, Q1, Q2, Q3, Q4, Q5, Q6, Q7]), "transformType" : TransformType.TRANSLATION_DISTANCE, "transformDirection" : qUnion([Q8]), "distance" : 25.4 * mm, "makeCopy" : false});
        }
        {
            var Q0;
            Q0=qCreatedBy(makeId("Top.planeOp"),FACE);
            var sketch = newSketch(context, id + "F12", { "sketchPlane" : qUnion([Q0])});
            skCircle(sketch, "E25", {"center": v(0, 0) * mm, "radius": 5.77 * mm});
            skCircle(sketch, "E26", {"center": v(0, 0) * mm, "radius": 10.74 * mm});
            skSolve(sketch);
        }
        {
            var Q0;
            Q0=makeQuery(id+"F12.imprint","IMPRINT",FACE,{"disambiguationData":[TD([[makeQuery(id+"F12.imprint","IMPRINT",EDGE,{"derivedFrom":sQuery(id+"F12.wireOp",EDGE,"E25")}),-1.0]])]});
            extrude(context, id + "F13", {"entities" : qUnion([Q0]), "operationType" : NewBodyOperationType.REMOVE, "depth" : 94.97 * mm});
        }
        {
            var Q0;
            Q0=makeQuery(id+"F3.opRevolve","SWEPT_FACE",FACE,{"disambiguationData":[OSD([sQuery(id+"F2.wireOp",EDGE,"E13")])]});
            cPlane(context, id + "F14", {"entities" : qUnion([Q0]), "cplaneType" : CPlaneType.OFFSET, "offset" : 0 * mm, "width" : 152.4 * mm, "height" : 152.4 * mm});
        }
        {
            var Q0;
            Q0=qCreatedBy(id+"F14.planeOp",FACE);
            var sketch = newSketch(context, id + "F15", { "sketchPlane" : qUnion([Q0])});
            skCircle(sketch, "E27", {"center": v(0, 0) * mm, "radius": 2.33 * mm});
            skSolve(sketch);
        }
        {
            var Q0;
            Q0=makeQuery(id+"F15.imprint","IMPRINT",FACE,{"disambiguationData":[TD([[makeQuery(id+"F15.imprint","IMPRINT",EDGE,{"derivedFrom":sQuery(id+"F15.wireOp",EDGE,"E27")}),1.0]])]});
            extrude(context, id + "F16", {"entities" : qUnion([Q0]), "depth" : 4.58 * mm, "hasDraft" : true, "draftAngle" : 18 * degree, "draftPullDirection" : true});
        }
        {
            var Q0;
            Q0=makeQuery(id+"F16.opExtrude","CAP_EDGE",EDGE,{"disambiguationData":[OSD([sQuery(id+"F15.wireOp",EDGE,"E27")])],"isStart":false});
            fillet(context, id + "F17", {"entities" : qUnion([Q0]), "radius" : 0.76 * mm, "tangentPropagation" : true, "allowEdgeOverflow" : false});
        }
    });
